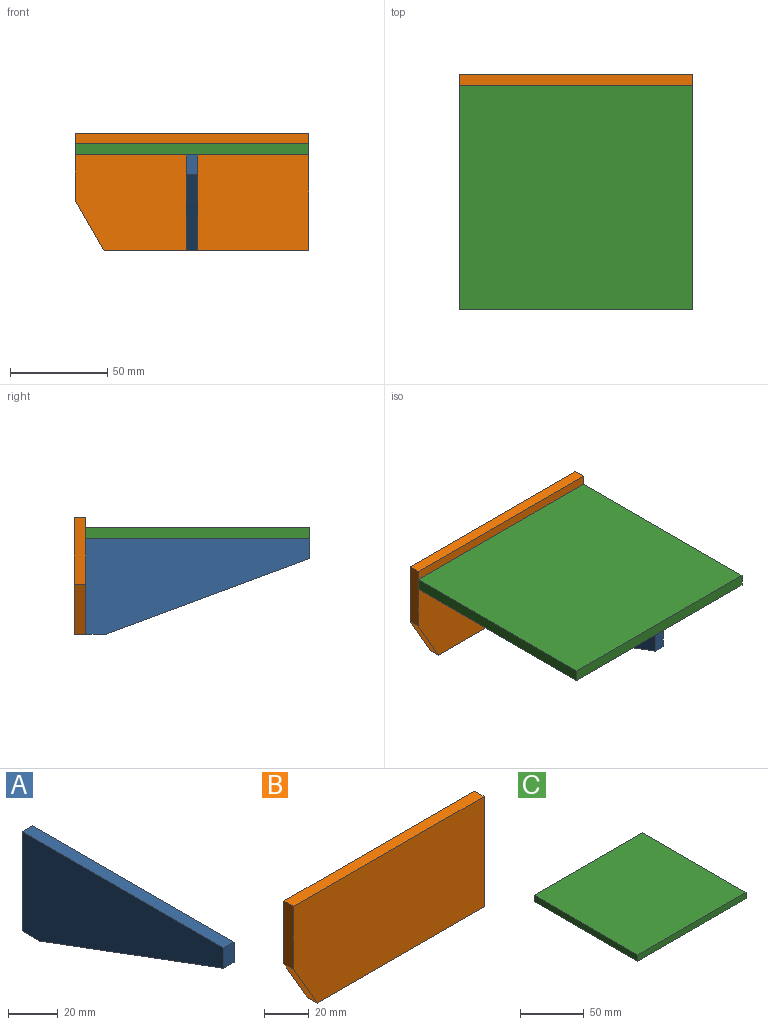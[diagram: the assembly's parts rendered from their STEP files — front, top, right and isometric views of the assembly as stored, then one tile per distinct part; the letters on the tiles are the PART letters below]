
ASSEMBLY  parts=3 mates=2
PART A: 7 faces, bbox 6x115x49 mm
  f0: plane 49x6mm, normal (0,1,0), area 294mm2, adj f1,f4,f5,f6
  f1: plane 115x6mm, normal (0,0,1), area 690mm2, adj f0,f2,f5,f6
  f2: plane 10x6mm, normal (0,-1,0), area 60mm2, adj f1,f3,f5,f6
  f3: plane 105x39mm, normal (0,-0.35,-0.94), area 672.1mm2, adj f2,f4,f5,f6
  f4: plane 10x6mm, normal (0,0,-1), area 60mm2, adj f0,f3,f5,f6
  f5: plane 115x49mm, normal (-1,0,0), area 3587.5mm2, adj f0,f1,f2,f3,f4
  f6: plane 115x49mm, normal (1,0,0), area 3587.5mm2, adj f0,f1,f2,f3,f4
PART B: 7 faces, bbox 120x6x60 mm
  f0: plane 105.15x6mm, normal (0,0,-1), area 630.9mm2, adj f3,f4,f5,f6
  f1: plane 120x6mm, normal (0,0,1), area 720mm2, adj f2,f3,f4,f5
  f2: plane 34.28x6mm, normal (-1,0,0), area 205.7mm2, adj f1,f4,f5,f6
  f3: plane 60x6mm, normal (1,0,0), area 360mm2, adj f0,f1,f4,f5
  f4: plane 120x60mm, normal (0,-1,0), area 7009.1mm2, adj f0,f1,f2,f3,f6
  f5: plane 120x60mm, normal (0,1,0), area 7009.1mm2, adj f0,f1,f2,f3,f6
  f6: plane 25.72x14.85mm, normal (-0.87,0,-0.5), area 178.2mm2, adj f0,f2,f4,f5
PART C: 6 faces, bbox 120x115x6 mm
  f0: plane 120x6mm, normal (0,1,0), area 720mm2, adj f1,f3,f4,f5
  f1: plane 115x6mm, normal (-1,0,0), area 690mm2, adj f0,f2,f4,f5
  f2: plane 120x6mm, normal (0,-1,0), area 720mm2, adj f1,f3,f4,f5
  f3: plane 115x6mm, normal (1,0,0), area 690mm2, adj f0,f2,f4,f5
  f4: plane 120x115mm, normal (0,0,1), area 13800mm2, adj f0,f1,f2,f3
  f5: plane 120x115mm, normal (0,0,-1), area 13800mm2, adj f0,f1,f2,f3
PLACE A at identity
PLACE B at identity fixed
PLACE C t=(0,-6,-11)mm
MATE fastened B.f4 <-> C.f0  axis (0,-1,0) through (120,-6,0)mm
MATE fastened A.f1 <-> C.f5  axis (0,0,1) through (57,-6,-11)mm
